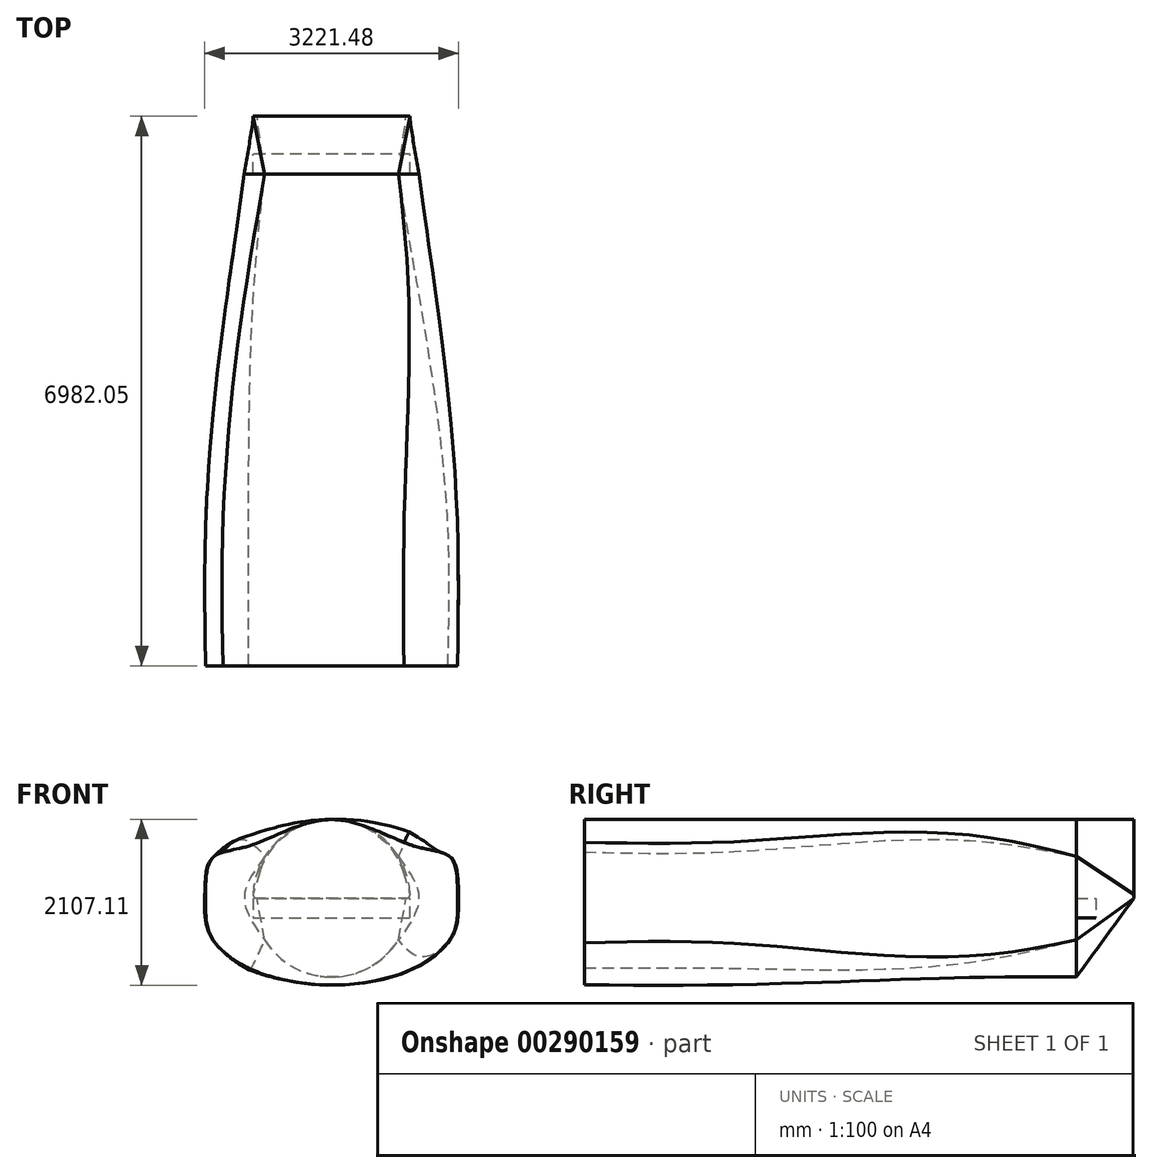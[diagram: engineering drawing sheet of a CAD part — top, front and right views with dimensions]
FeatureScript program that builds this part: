
annotation { "Feature Type Name" : "Feature", "Feature Type Description" : "" }
export const myFeature = defineFeature(function(context is Context, id is Id, definition is map)
    precondition{}
    {
        {
            var Q0;
            Q0=qCreatedBy(makeId("Front.planeOp"),FACE);
            var sketch = newSketch(context, id + "F0", { "sketchPlane" : qUnion([Q0])});
            skPoint(sketch, "E0.middle", {"position": v(0, 0) * mm});
            skFitSpline(sketch, "E1", {"points": [v(0, 1000) * mm, v(1060, 662.5) * mm, v(1517.6, 506.84) * mm, v(1600, 0) * mm, v(1517.6, -506.84) * mm, v(750, -1000) * mm, v(-750, -1000) * mm, v(-1517.6, -506.84) * mm, v(-1600, 0) * mm, v(-1517.6, 506.84) * mm, v(-1060, 662.5) * mm, v(0, 1000) * mm]});
            skSolve(sketch);
        }
        {
            var Q0;
            Q0=qCreatedBy(makeId("Front.planeOp"),FACE);
            cPlane(context, id + "F1", {"entities" : qUnion([Q0]), "cplaneType" : CPlaneType.OFFSET, "offset" : 1750 * mm, "width" : 150 * mm, "height" : 150 * mm});
        }
        {
            var Q0;
            Q0=qCreatedBy(id+"F1.planeOp",FACE);
            var sketch = newSketch(context, id + "F2", { "sketchPlane" : qUnion([Q0])});
            skPoint(sketch, "E2.middle", {"position": v(0, 0) * mm});
            skFitSpline(sketch, "E3", {"points": [v(0, 1000) * mm, v(1060, 662.5) * mm, v(1517.6, 506.84) * mm, v(1600, 0) * mm, v(1517.6, -506.84) * mm, v(750, -1000) * mm, v(-750, -1000) * mm, v(-1517.6, -506.84) * mm, v(-1600, 0) * mm, v(-1517.6, 506.84) * mm, v(-1060, 662.5) * mm, v(0, 1000) * mm]});
            skSolve(sketch);
        }
        {
            var Q0;
            Q0=qCreatedBy(makeId("Front.planeOp"),FACE);
            cPlane(context, id + "F3", {"entities" : qUnion([Q0]), "cplaneType" : CPlaneType.OFFSET, "offset" : 3500 * mm, "oppositeDirection" : true, "width" : 150 * mm, "height" : 150 * mm});
        }
        {
            var Q0;
            Q0=qCreatedBy(id+"F3.planeOp",FACE);
            var sketch = newSketch(context, id + "F4", { "sketchPlane" : qUnion([Q0])});
            skPoint(sketch, "E4.middle", {"position": v(0, 0) * mm});
            skFitSpline(sketch, "E5", {"points": [v(0, 1000) * mm, v(1060, 662.5) * mm, v(1250, 0) * mm, v(1060, -662.5) * mm, v(0, -1000) * mm, v(-1060, -662.5) * mm, v(-1250, 0) * mm, v(-1060, 662.5) * mm, v(0, 1000) * mm]});
            skSolve(sketch);
        }
        {
            var Q0;
            Q0=qCreatedBy(makeId("Front.planeOp"),FACE);
            cPlane(context, id + "F5", {"entities" : qUnion([Q0]), "cplaneType" : CPlaneType.OFFSET, "offset" : 4500 * mm, "oppositeDirection" : true, "width" : 150 * mm, "height" : 150 * mm});
        }
        {
            var Q0;
            Q0=qCreatedBy(id+"F5.planeOp",FACE);
            var sketch = newSketch(context, id + "F6", { "sketchPlane" : qUnion([Q0])});
            skPoint(sketch, "E6.middle", {"position": v(0, 0) * mm});
            skArc(sketch, "E7", {"start": v(848, 530) * mm, "mid": v(0, 1000) * mm, "end": v(-848, 530) * mm});
            skFitSpline(sketch, "E8", {"points": [v(848, 530) * mm, v(1108.5, 0) * mm, v(848, -530) * mm], "startDerivative": vector(781.5, -1060) * mm, "endDerivative": vector(-781.5, -1060) * mm});
            skFitSpline(sketch, "E9", {"points": [v(-848, 530) * mm, v(-1108.5, 0) * mm, v(-848, -530) * mm], "startDerivative": vector(-781.5, -1060) * mm, "endDerivative": vector(781.5, -1060) * mm});
            skArc(sketch, "E10.trimOffspring", {"start": v(-848, -530) * mm, "mid": v(0, -1000) * mm, "end": v(848, -530) * mm});
            skSolve(sketch);
        }
        {
            var Q0;
            Q0=makeQuery(id+"F2.imprint","IMPRINT",FACE,{"disambiguationData":[TD([[makeQuery(id+"F2.imprint","IMPRINT",EDGE,{"derivedFrom":sQuery(id+"F2.wireOp",EDGE,"E3")}),-1.0]])]});
            var Q1;
            Q1=makeQuery(id+"F0.imprint","IMPRINT",FACE,{"disambiguationData":[TD([[makeQuery(id+"F0.imprint","IMPRINT",EDGE,{"derivedFrom":sQuery(id+"F0.wireOp",EDGE,"E1")}),-1.0]])]});
            var Q2;
            Q2=makeQuery(id+"F4.imprint","IMPRINT",FACE,{"disambiguationData":[TD([[makeQuery(id+"F4.imprint","IMPRINT",EDGE,{"derivedFrom":sQuery(id+"F4.wireOp",EDGE,"E5")}),-1.0]])]});
            var Q3;
            Q3=makeQuery(id+"F6.imprint","IMPRINT",FACE,{"disambiguationData":[TD([[makeQuery(id+"F6.imprint","IMPRINT",EDGE,{"derivedFrom":sQuery(id+"F6.wireOp",EDGE,"E7")}),1.0]])]});
            loft(context, id + "F7", {"sheetProfilesArray" : [{ "sheetProfileEntities" : qUnion([Q0]) }, { "sheetProfileEntities" : qUnion([Q1]) }, { "sheetProfileEntities" : qUnion([Q2]) }, { "sheetProfileEntities" : qUnion([Q3]) }]});
        }
        {
            var Q0;
            Q0=qCreatedBy(makeId("Front.planeOp"),FACE);
            cPlane(context, id + "F8", {"entities" : qUnion([Q0]), "cplaneType" : CPlaneType.OFFSET, "offset" : 5232.05 * mm, "oppositeDirection" : true, "width" : 150 * mm, "height" : 150 * mm});
        }
        {
            var Q0;
            Q0=qCreatedBy(id+"F8.planeOp",FACE);
            var sketch = newSketch(context, id + "F9", { "sketchPlane" : qUnion([Q0])});
            skArc(sketch, "E11", {"start": v(998.61, 52.63) * mm, "mid": v(0, 1000) * mm, "end": v(-998.61, 52.63) * mm});
            skLineSegment(sketch, "E12", {"start": v(-948.68, 0) * mm, "end": v(948.68, 0) * mm});
            skPoint(sketch, "E13.visualSharp", {"position": v(-1000, 0) * mm});
            skArc(sketch, "E13.filletArc", {"start": v(-998.61, 52.63) * mm, "mid": v(-984.96, 15.59) * mm, "end": v(-948.68, 0) * mm});
            skPoint(sketch, "E14.visualSharp", {"position": v(1000, 0) * mm});
            skArc(sketch, "E14.filletArc", {"start": v(948.68, 0) * mm, "mid": v(984.96, 15.59) * mm, "end": v(998.61, 52.63) * mm});
            skSolve(sketch);
        }
        {
            var Q0;
            Q0=qCreatedBy(makeId("Front.planeOp"),FACE);
            cPlane(context, id + "F10", {"entities" : qUnion([Q0]), "cplaneType" : CPlaneType.OFFSET, "offset" : 4750 * mm, "oppositeDirection" : true, "width" : 150 * mm, "height" : 150 * mm});
        }
        {
            var Q0;
            Q0=qCreatedBy(makeId("Front.planeOp"),FACE);
            cPlane(context, id + "F11", {"entities" : qUnion([Q0]), "cplaneType" : CPlaneType.OFFSET, "offset" : 4750 * mm, "oppositeDirection" : true, "width" : 150 * mm, "height" : 150 * mm});
        }
        {
            var Q0;
            Q0=qCreatedBy(id+"F11.planeOp",FACE);
            var sketch = newSketch(context, id + "F12", { "sketchPlane" : qUnion([Q0])});
            skLineSegment(sketch, "E15", {"start": v(0, 0) * mm, "end": v(-1000, 0) * mm});
            skLineSegment(sketch, "E16", {"start": v(-1000, 0) * mm, "end": v(-1000, -250) * mm});
            skLineSegment(sketch, "E17", {"start": v(-1000, -250) * mm, "end": v(1000, -250) * mm});
            skLineSegment(sketch, "E18", {"start": v(1000, -250) * mm, "end": v(1000, 0) * mm});
            skLineSegment(sketch, "E19", {"start": v(1000, 0) * mm, "end": v(0, 0) * mm});
            skSolve(sketch);
        }
        {
            var Q0;
            Q0=makeQuery(id+"F12.imprint","IMPRINT",FACE,{"disambiguationData":[TD([[makeQuery(id+"F12.imprint","IMPRINT",EDGE,{"derivedFrom":sQuery(id+"F12.wireOp",EDGE,"E15")}),1.0]])]});
            extrude(context, id + "F13", {"entities" : qUnion([Q0]), "depth" : 250 * mm});
        }
        {
            var Q0;
            Q0=makeQuery(id+"F6.imprint","IMPRINT",FACE,{"disambiguationData":[TD([[makeQuery(id+"F6.imprint","IMPRINT",EDGE,{"derivedFrom":sQuery(id+"F6.wireOp",EDGE,"E7")}),1.0]])]});
            var Q1;
            Q1=makeQuery(id+"F9.imprint","IMPRINT",FACE,{"disambiguationData":[TD([[makeQuery(id+"F9.imprint","IMPRINT",EDGE,{"derivedFrom":sQuery(id+"F9.wireOp",EDGE,"E11")}),1.0]])]});
            loft(context, id + "F14", {"sheetProfilesArray" : [{ "sheetProfileEntities" : qUnion([Q0]) }, { "sheetProfileEntities" : qUnion([Q1]) }]});
        }
    });
